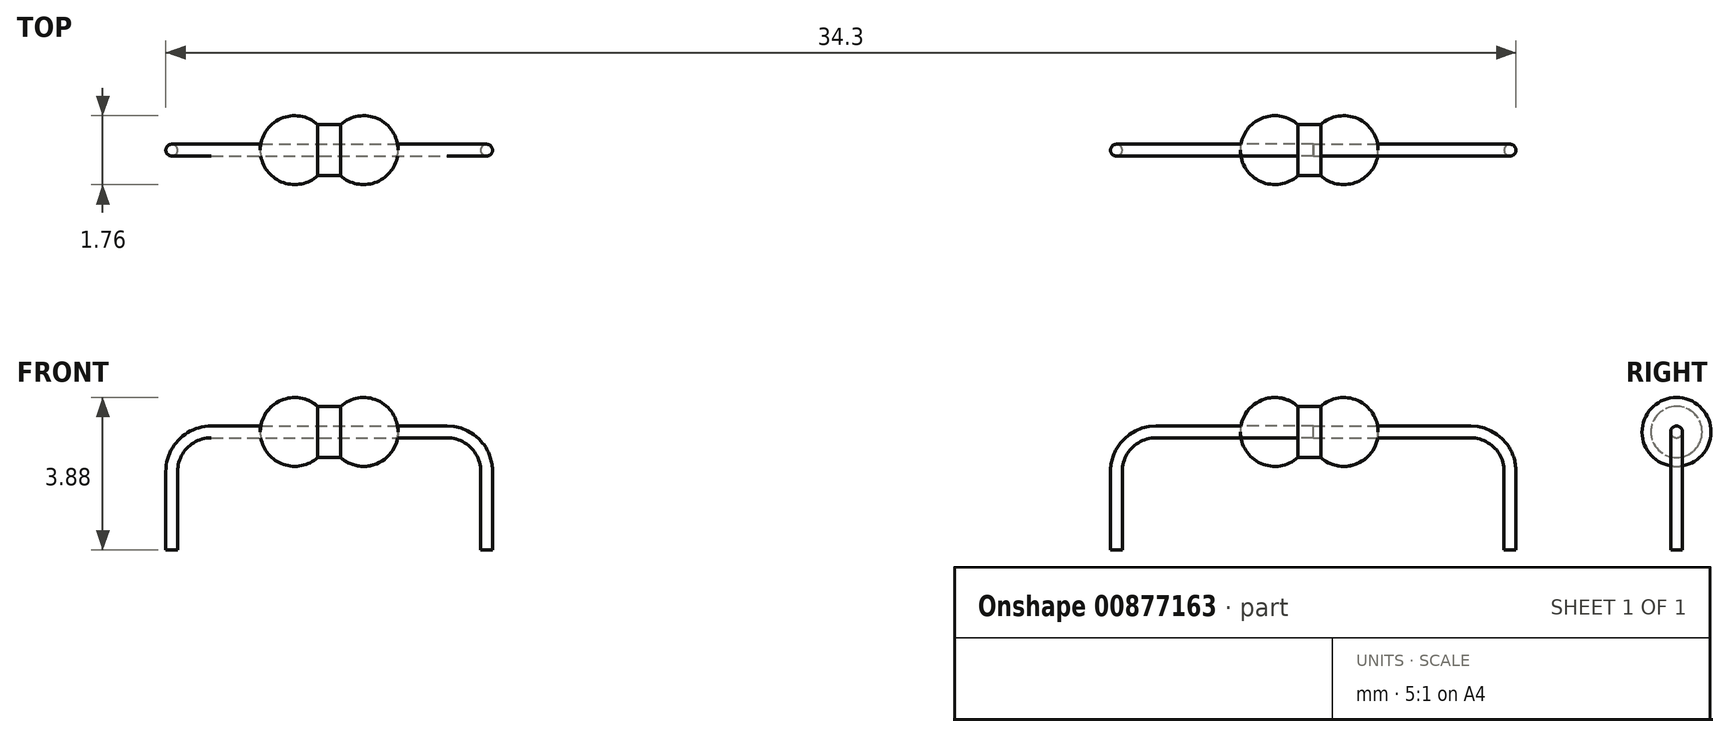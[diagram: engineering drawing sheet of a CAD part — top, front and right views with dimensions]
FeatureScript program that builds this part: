
annotation { "Feature Type Name" : "Feature", "Feature Type Description" : "" }
export const myFeature = defineFeature(function(context is Context, id is Id, definition is map)
    precondition{}
    {
        {
            var Q0;
            Q0=qCreatedBy(makeId("Front.planeOp"),FACE);
            var sketch = newSketch(context, id + "F0", { "sketchPlane" : qUnion([Q0])});
            skLineSegment(sketch, "E0.bottom", {"start": v(0.88, -0.65) * mm, "end": v(-0.88, -0.65) * mm});
            skLineSegment(sketch, "E0.top", {"start": v(0.88, 0.65) * mm, "end": v(-0.88, 0.65) * mm});
            skLineSegment(sketch, "E0.left", {"start": v(0.88, -0.65) * mm, "end": v(0.88, 0.65) * mm});
            skLineSegment(sketch, "E0.right", {"start": v(-0.87, -0.65) * mm, "end": v(-0.87, 0.65) * mm});
            skPoint(sketch, "E0.middle", {"position": v(0, 0) * mm});
            skCircle(sketch, "E1", {"center": v(0.88, 0) * mm, "radius": 0.88 * mm});
            skCircle(sketch, "E2", {"center": v(-0.87, 0) * mm, "radius": 0.88 * mm});
            skLineSegment(sketch, "E3", {"start": v(-1.75, 0) * mm, "end": v(1.75, 0) * mm});
            skSolve(sketch);
        }
        {
            var Q0;
            {var subQ0=sQuery(id+"F0.wireOp",EDGE,"E0.right");var subQ1=sQuery(id+"F0.wireOp",EDGE,"E0.top");var subQ2=makeQuery(id+"F0.imprint","INTERSECT",VERTEX,{"derivedFrom":[subQ1,subQ0]});Q0=makeQuery(id+"F0.imprint","IMPRINT",FACE,{"disambiguationData":[TD([[makeQuery(id+"F0.imprint","IMPRINT",EDGE,{"disambiguationData":[TD([[subQ2,1.0]])],"derivedFrom":subQ1}),-1.0]])]});}
            var Q1;
            {var subQ0=sQuery(id+"F0.wireOp",EDGE,"E0.right");var subQ1=sQuery(id+"F0.wireOp",EDGE,"E0.top");var subQ2=makeQuery(id+"F0.imprint","INTERSECT",VERTEX,{"derivedFrom":[subQ1,subQ0]});Q1=makeQuery(id+"F0.imprint","IMPRINT",FACE,{"disambiguationData":[TD([[makeQuery(id+"F0.imprint","IMPRINT",EDGE,{"disambiguationData":[TD([[subQ2,1.0]])],"derivedFrom":subQ1}),1.0]])]});}
            var Q2;
            {var subQ0=sQuery(id+"F0.wireOp",EDGE,"E1");var subQ1=sQuery(id+"F0.wireOp",EDGE,"E0.top");var subQ2=makeQuery(id+"F0.imprint","INTERSECT",VERTEX,{"derivedFrom":[subQ1,subQ0]});Q2=makeQuery(id+"F0.imprint","IMPRINT",FACE,{"disambiguationData":[TD([[makeQuery(id+"F0.imprint","IMPRINT",EDGE,{"disambiguationData":[TD([[subQ2,-1.0]])],"derivedFrom":subQ1}),1.0]])]});}
            var Q3;
            {var subQ0=sQuery(id+"F0.wireOp",EDGE,"E0.left");var subQ1=sQuery(id+"F0.wireOp",EDGE,"E0.top");var subQ2=makeQuery(id+"F0.imprint","INTERSECT",VERTEX,{"derivedFrom":[subQ1,subQ0]});Q3=makeQuery(id+"F0.imprint","IMPRINT",FACE,{"disambiguationData":[TD([[makeQuery(id+"F0.imprint","IMPRINT",EDGE,{"disambiguationData":[TD([[subQ2,-1.0]])],"derivedFrom":subQ1}),1.0]])]});}
            var Q4;
            {var subQ0=sQuery(id+"F0.wireOp",EDGE,"E0.left");var subQ1=sQuery(id+"F0.wireOp",EDGE,"E0.top");var subQ2=makeQuery(id+"F0.imprint","INTERSECT",VERTEX,{"derivedFrom":[subQ1,subQ0]});Q4=makeQuery(id+"F0.imprint","IMPRINT",FACE,{"disambiguationData":[TD([[makeQuery(id+"F0.imprint","IMPRINT",EDGE,{"disambiguationData":[TD([[subQ2,-1.0]])],"derivedFrom":subQ1}),-1.0]])]});}
            var Q5;
            Q5=sQuery(id+"F0.wireOp",EDGE,"E3");
            revolve(context, id + "F1", {"surfaceOperationType" : NewSurfaceOperationType.NEW, "entities" : qUnion([Q0, Q1, Q2, Q3, Q4]), "axis" : qUnion([Q5]), "revolveType" : RevolveType.FULL});
        }
        {
            var Q0;
            Q0=qCreatedBy(makeId("Front.planeOp"),FACE);
            var sketch = newSketch(context, id + "F2", { "sketchPlane" : qUnion([Q0])});
            skLineSegment(sketch, "E4", {"start": v(0, 0) * mm, "end": v(-3, 0) * mm});
            skLineSegment(sketch, "E5", {"start": v(0, 0) * mm, "end": v(3, 0) * mm});
            skArc(sketch, "E6", {"start": v(-3, 0) * mm, "mid": v(-3.7, -0.3) * mm, "end": v(-4, -1) * mm});
            skArc(sketch, "E7", {"start": v(4, -1) * mm, "mid": v(3.7, -0.3) * mm, "end": v(3, 0) * mm});
            skLineSegment(sketch, "E8", {"start": v(-4, -1) * mm, "end": v(-4, -3) * mm});
            skLineSegment(sketch, "E9", {"start": v(4, -1) * mm, "end": v(4, -3) * mm});
            skSolve(sketch);
        }
        {
            var Q0;
            Q0=qCreatedBy(makeId("Right.planeOp"),FACE);
            var sketch = newSketch(context, id + "F3", { "sketchPlane" : qUnion([Q0])});
            skCircle(sketch, "E10", {"center": v(0, 0) * mm, "radius": 0.15 * mm});
            skSolve(sketch);
        }
        {
            var Q0;
            Q0 = qSketchRegion(id + "F3", true);
            var Q1;
            Q1 = qConstructionFilter(qBodyType(qCreatedBy(id + "F2" ,EDGE), BodyType.WIRE), ConstructionObject.NO);
            sweep(context, id + "F4", {"profiles" : qUnion([Q0]), "path" : qUnion([Q1])});
        }
        {
            var Q0;
            Q0=qCreatedBy(makeId("Right.planeOp"),FACE);
            cPlane(context, id + "F5", {"entities" : qUnion([Q0]), "cplaneType" : CPlaneType.OFFSET, "offset" : 25 * mm, "width" : 150 * mm, "height" : 150 * mm});
        }
        {
            var Q0;
            Q0=qCreatedBy(makeId("Front.planeOp"),FACE);
            var sketch = newSketch(context, id + "F6", { "sketchPlane" : qUnion([Q0])});
            skLineSegment(sketch, "E11", {"start": v(25, 0) * mm, "end": v(21, 0) * mm});
            skLineSegment(sketch, "E12", {"start": v(20, -1) * mm, "end": v(20, -3) * mm});
            skArc(sketch, "E13", {"start": v(21, 0) * mm, "mid": v(20.3, -0.3) * mm, "end": v(20, -1) * mm});
            skSolve(sketch);
        }
        {
            var Q0;
            Q0=qCreatedBy(id+"F5.planeOp",FACE);
            var sketch = newSketch(context, id + "F7", { "sketchPlane" : qUnion([Q0])});
            skCircle(sketch, "E14", {"center": v(0, 0) * mm, "radius": 0.15 * mm});
            skSolve(sketch);
        }
        {
            var Q0;
            Q0=makeQuery(id+"F7.imprint","IMPRINT",FACE,{"disambiguationData":[TD([[makeQuery(id+"F7.imprint","IMPRINT",EDGE,{"derivedFrom":sQuery(id+"F7.wireOp",EDGE,"E14")}),1.0]])]});
            var Q1;
            Q1=sQuery(id+"F6.wireOp",EDGE,"E11");
            var Q2;
            Q2=sQuery(id+"F6.wireOp",EDGE,"E13");
            var Q3;
            Q3=sQuery(id+"F6.wireOp",EDGE,"E12");
            sweep(context, id + "F8", {"profiles" : qUnion([Q0]), "path" : qUnion([Q1, Q2, Q3])});
        }
        {
            var Q0;
            Q0=makeQuery(id+"F8.opSweep","SWEPT_BODY",BODY,{"disambiguationData":[OSD([sQuery(id+"F6.wireOp",EDGE,"E12"),sQuery(id+"F7.wireOp",EDGE,"E14")])]});
            var Q1;
            Q1=makeQuery(id+"F8.opSweep","CAP_FACE",FACE,{"disambiguationData":[OSD([sQuery(id+"F6.wireOp",VERTEX,"E11.start"),sQuery(id+"F7.wireOp",EDGE,"E14")])],"isStart":true});
            mirror(context, id + "F9", {"operationType" : NewBodyOperationType.ADD, "entities" : qUnion([Q0]), "mirrorPlane" : qUnion([Q1])});
        }
        {
            var Q0;
            Q0=makeQuery(id+"F1.opRevolve","SWEPT_BODY",BODY,{"disambiguationData":[OSD([sQuery(id+"F0.wireOp",EDGE,"E0.top"),sQuery(id+"F0.wireOp",EDGE,"E1"),sQuery(id+"F0.wireOp",EDGE,"E2"),sQuery(id+"F0.wireOp",EDGE,"E3")])]});
            transform(context, id + "F10", {"entities" : qUnion([Q0]), "transformType" : TransformType.TRANSLATION_3D, "dx" : 24.9 * mm, "dy" : 0 * mm, "dz" : 0 * mm, "makeCopy" : true});
        }
    });
